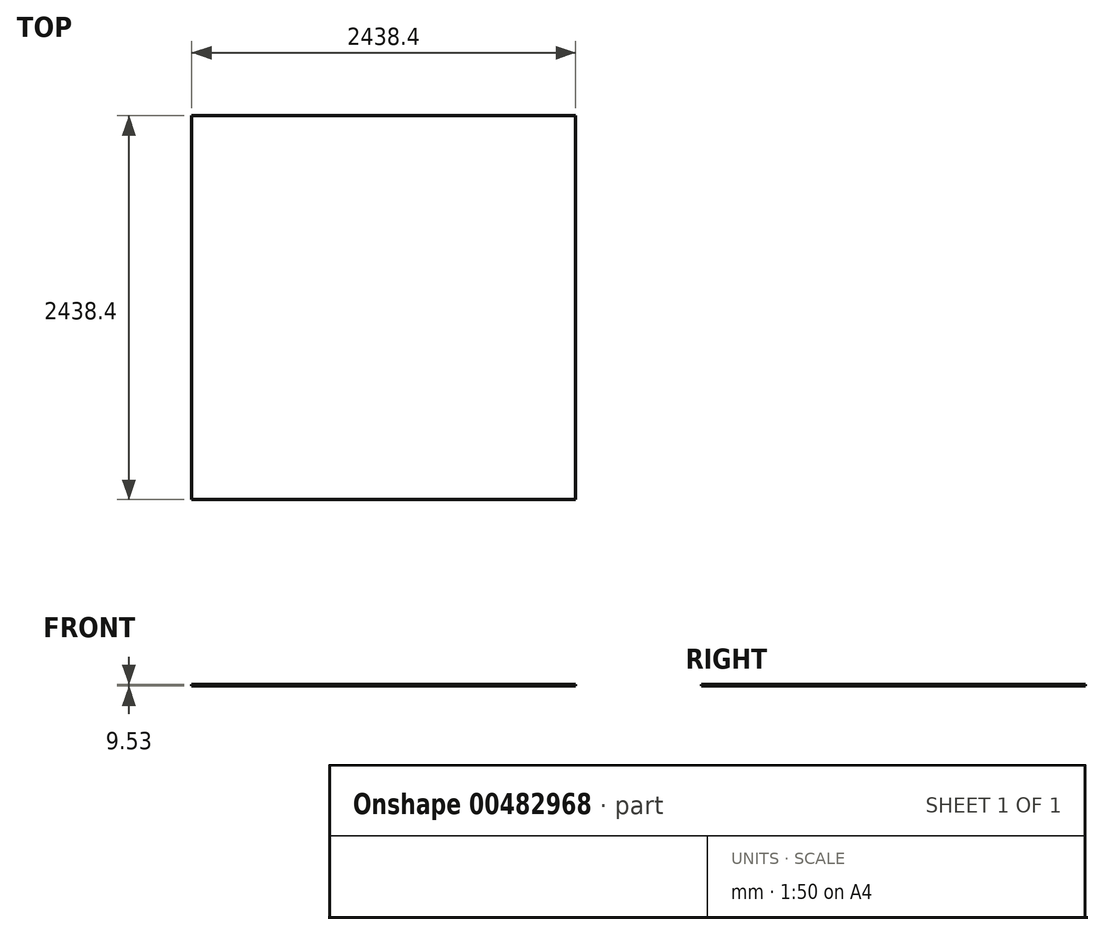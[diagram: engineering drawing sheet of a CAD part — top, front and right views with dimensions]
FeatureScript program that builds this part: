
annotation { "Feature Type Name" : "Feature", "Feature Type Description" : "" }
export const myFeature = defineFeature(function(context is Context, id is Id, definition is map)
    precondition{}
    {
        {
            var Q0;
            Q0=qCreatedBy(makeId("Top.planeOp"),FACE);
            var sketch = newSketch(context, id + "F0", { "sketchPlane" : qUnion([Q0])});
            skLineSegment(sketch, "E0.bottom", {"start": v(0, 0) * mm, "end": v(2438.4, 0) * mm});
            skLineSegment(sketch, "E0.top", {"start": v(0, -2438.4) * mm, "end": v(2438.4, -2438.4) * mm});
            skLineSegment(sketch, "E0.left", {"start": v(0, 0) * mm, "end": v(0, -2438.4) * mm});
            skLineSegment(sketch, "E0.right", {"start": v(2438.4, 0) * mm, "end": v(2438.4, -2438.4) * mm});
            skSolve(sketch);
        }
        {
            var Q0;
            Q0=makeQuery(id+"F0.imprint","IMPRINT",FACE,{"disambiguationData":[TD([[makeQuery(id+"F0.imprint","IMPRINT",EDGE,{"derivedFrom":sQuery(id+"F0.wireOp",EDGE,"E0.bottom")}),-1.0]])]});
            extrude(context, id + "F1", {"entities" : qUnion([Q0]), "depth" : 9.52 * mm});
        }
    });
